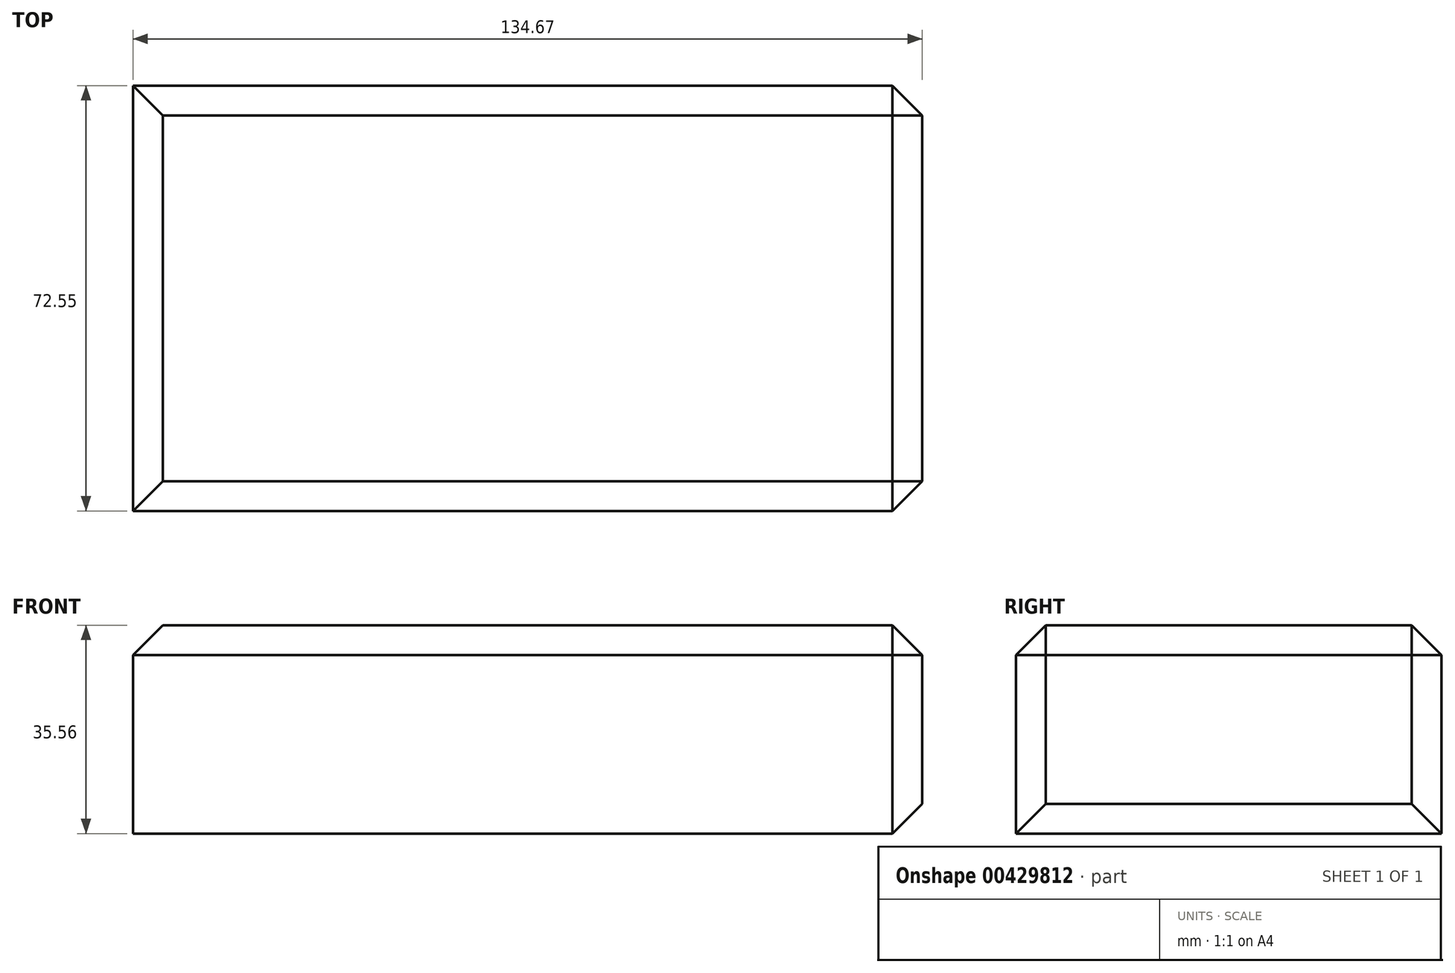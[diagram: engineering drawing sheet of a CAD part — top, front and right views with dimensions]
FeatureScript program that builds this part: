
annotation { "Feature Type Name" : "Feature", "Feature Type Description" : "" }
export const myFeature = defineFeature(function(context is Context, id is Id, definition is map)
    precondition{}
    {
        {
            var Q0;
            Q0=qCreatedBy(makeId("Top.planeOp"),FACE);
            var sketch = newSketch(context, id + "F0", { "sketchPlane" : qUnion([Q0])});
            skLineSegment(sketch, "E0.bottom", {"start": v(-19.47, -14.49) * mm, "end": v(115.2, -14.49) * mm});
            skLineSegment(sketch, "E0.top", {"start": v(-19.47, -87.04) * mm, "end": v(115.2, -87.04) * mm});
            skLineSegment(sketch, "E0.left", {"start": v(-19.47, -14.49) * mm, "end": v(-19.47, -87.04) * mm});
            skLineSegment(sketch, "E0.right", {"start": v(115.2, -14.49) * mm, "end": v(115.2, -87.04) * mm});
            skSolve(sketch);
        }
        {
            var Q0;
            Q0 = qSketchRegion(id + "F0", true);
            extrude(context, id + "F1", {"entities" : qUnion([Q0]), "depth" : 35.56 * mm});
        }
        {
            var Q0;
            Q0=makeQuery(id+"F1.opExtrude","CAP_FACE",FACE,{"disambiguationData":[OSD([sQuery(id+"F0.wireOp",EDGE,"E0.bottom"),sQuery(id+"F0.wireOp",EDGE,"E0.top"),sQuery(id+"F0.wireOp",EDGE,"E0.left"),sQuery(id+"F0.wireOp",EDGE,"E0.right")])],"isStart":false});
            var Q1;
            Q1=makeQuery(id+"F1.opExtrude","SWEPT_FACE",FACE,{"disambiguationData":[OSD([sQuery(id+"F0.wireOp",EDGE,"E0.right")])]});
            chamfer(context, id + "F2", {"entities" : qUnion([Q0, Q1]), "width" : 5.08 * mm, "tangentPropagation" : true});
        }
    });
